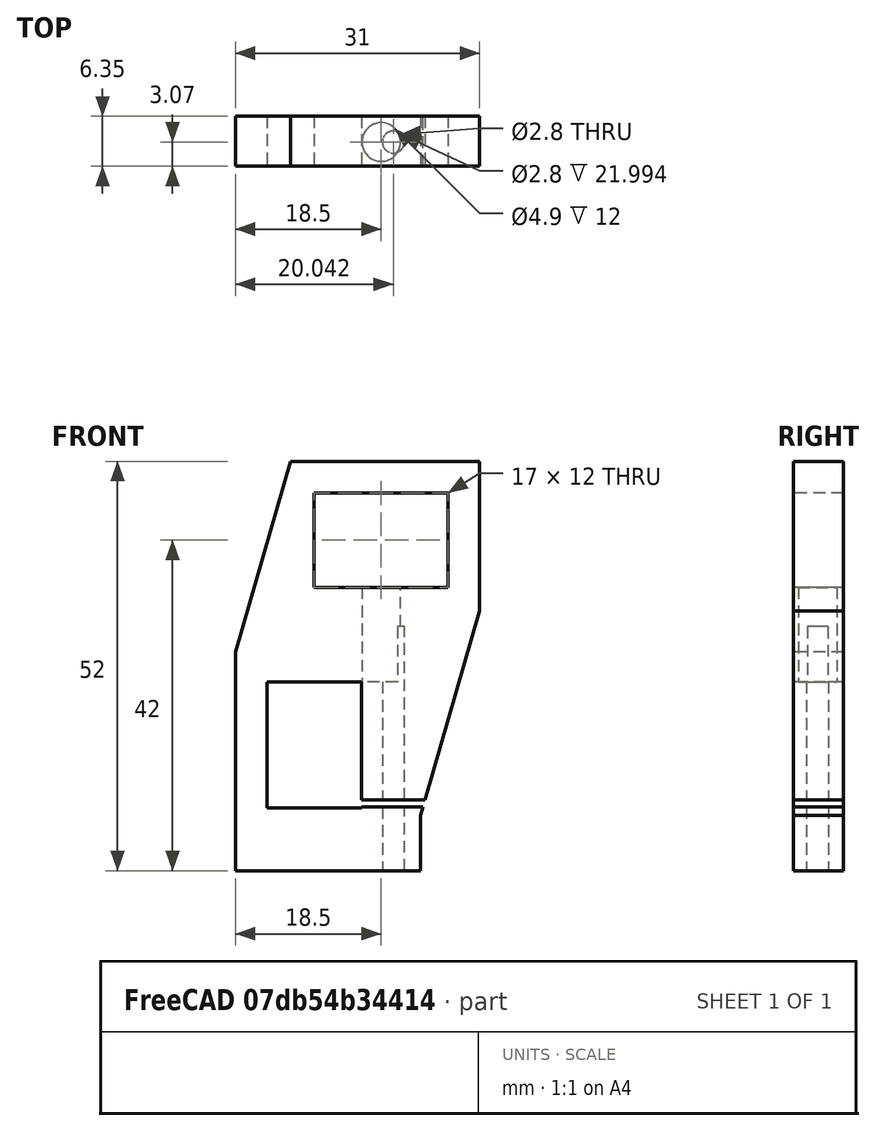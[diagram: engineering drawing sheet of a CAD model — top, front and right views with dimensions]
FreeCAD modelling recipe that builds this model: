
FCSTD DOCUMENT  (FreeCAD 0.19R)
Label: Tensioner_rail_clamp
License: All rights reserved
LicenseURL: http://en.wikipedia.org/wiki/All_rights_reserved
objects: Sketcher::SketchObject×4, PartDesign::Pocket×3, PartDesign::Pad×1, PartDesign::Body×1, Mesh::Feature×1
note: 13 computed .brp shape members not serialized (recipe doc carries the construction recipe); baked Part::Feature solids carry a one-line shape summary decoded from their .brp

FEATURE [Sketcher::SketchObject] Sketch
  FullyConstrained = false
  MapMode = 5
  Placement = pos=(0,0,0) rot=(1,0,0;1.5708rad)
  Support = -> [XZ_Plane]
  sketch-geometry (21):
    g0: LineSegment StartX=-8.5 StartY=6 StartZ=0 EndX=8.5 EndY=6 EndZ=0
    g1: LineSegment StartX=8.5 StartY=6 StartZ=0 EndX=8.5 EndY=-6 EndZ=0
    g2: LineSegment StartX=8.5 StartY=-6 StartZ=0 EndX=-8.5 EndY=-6 EndZ=0
    g3: LineSegment StartX=-8.5 StartY=-6 StartZ=0 EndX=-8.5 EndY=6 EndZ=0
    g4: LineSegment StartX=-11.5092 StartY=10 StartZ=0 EndX=12.5 EndY=10 EndZ=0
    g5: LineSegment StartX=12.5 StartY=10 StartZ=0 EndX=12.5 EndY=-9 EndZ=0
    g6: LineSegment StartX=5 StartY=-42 StartZ=0 EndX=-18.5 EndY=-42 EndZ=0
    g7: LineSegment StartX=-18.5 StartY=-42 StartZ=0 EndX=-18.5 EndY=-14.2346 EndZ=0
    g8: LineSegment StartX=-14.5 StartY=-18 StartZ=0 EndX=-2.5 EndY=-18 EndZ=0
    g9: LineSegment StartX=-2.5 StartY=-18 StartZ=0 EndX=-2.5 EndY=-34 EndZ=0
    g10: LineSegment StartX=-2.5 StartY=-34 StartZ=0 EndX=-14.5 EndY=-34 EndZ=0
    g11: LineSegment StartX=-14.5 StartY=-34 StartZ=0 EndX=-14.5 EndY=-18 EndZ=0
    g12: LineSegment StartX=-8.5 StartY=-12.9672 StartZ=0 EndX=-8.5 EndY=-37.1721 EndZ=0
    g13: LineSegment StartX=-22 StartY=-34 StartZ=0 EndX=5 EndY=-34 EndZ=0
    g14: LineSegment StartX=5 StartY=-34 StartZ=0 EndX=5 EndY=-46.7 EndZ=0
    g15: LineSegment StartX=5 StartY=-46.7 StartZ=0 EndX=-22 EndY=-46.7 EndZ=0
    g16: LineSegment StartX=-22 StartY=-46.7 StartZ=0 EndX=-22 EndY=-34 EndZ=0
    g17: LineSegment StartX=-8.5 StartY=-41.244 StartZ=0 EndX=-8.5 EndY=-73.7754 EndZ=0
    g18: LineSegment StartX=-18.5 StartY=-14.2346 StartZ=0 EndX=-11.5092 EndY=10 EndZ=0
    g19: LineSegment StartX=5 StartY=-42 StartZ=0 EndX=5 EndY=-35 EndZ=0
    g20: LineSegment StartX=5 StartY=-35 StartZ=0 EndX=12.5 EndY=-9 EndZ=0
  constraints (57):
    c: Coincident(g1,g2)
    c: Coincident(g2,g3)
    c: Coincident(g3,g0)
    c: Horizontal(g2)
    c: Vertical(g1)
    c: Distance(g0) = 17
    c: Coincident(g0,g1)
    c: Symmetric(g0,g2,g-1)
    c: Symmetric(g1,g0,g-1)
    c: Distance(g1) = 12
    c: Horizontal(g4)
    c: Coincident(g4,g5)
    c: Vertical(g5)
    c: Horizontal(g6)
    c: Coincident(g6,g7)
    c: Vertical(g7)
    c: Coincident(g8,g9)
    c: Coincident(g9,g10)
    c: Coincident(g10,g11)
    c: Coincident(g11,g8)
    c: Horizontal(g8)
    c: Horizontal(g10)
    c: Vertical(g9)
    c: Vertical(g11)
    c: Distance(g9) = 16
    c: Distance(g8) = 12
    c: Symmetric(g10,g9,g12)
    c: Coincident(g13,g14)
    c: Coincident(g14,g15)
    c: Coincident(g15,g16)
    c: Coincident(g16,g13)
    c: Horizontal(g13)
    c: Horizontal(g15)
    c: Vertical(g14)
    c: Vertical(g16)
    c: Symmetric(g13,g13,g17)
    c: Distance(g13) = 27
    c: Distance(g14) = 12.7
    c: DistanceX(g-1,g13) = 5
    c: PointOnObject(g12,g17)
    c: Distance(g10,g7) = 4
    c: Distance(g0,g4) = 4
    c: Distance(g9,g6) = 8
    c: Coincident(g7,g18)
    c: Coincident(g18,g4)
    c: Distance(g4,g1) = 4
    c: Coincident(g6,g19)
    c: Vertical(g19)
    c: Coincident(g19,g20)
    c: Coincident(g20,g5)
    c: Parallel(g20,g18)
    c: DistanceY(g8,g0) = 24
    c: Distance(g0,g18) = 4
    c: PointOnObject(g9,g13)
    c: DistanceX(g6) = 5
    c: DistanceY(g5) = -9
    c: DistanceY(g19) = -35
FEATURE [PartDesign::Pad] Pad
  Direction = (1,1,1)
  Length = 6.35
  Length2 = 100
  Placement = pos=(0,0,0) rot=(1,0,0;1.5708rad)
  Profile = -> Sketch
  Type = 0
FEATURE [Sketcher::SketchObject] Sketch001
  FullyConstrained = false
  MapMode = 5
  Placement = pos=(0,-6.35,4.2e-15) rot=(1,0,0;1.5708rad)
  Support = -> [Pad]
  sketch-geometry (4):
    g0: LineSegment StartX=-2.64152 StartY=-32.9944 StartZ=0 EndX=6.5725 EndY=-32.9944 EndZ=0
    g1: LineSegment StartX=6.5725 StartY=-32.9944 StartZ=0 EndX=6.5725 EndY=-33.8968 EndZ=0
    g2: LineSegment StartX=6.5725 StartY=-33.8968 StartZ=0 EndX=-2.64152 EndY=-33.8968 EndZ=0
    g3: LineSegment StartX=-2.64152 StartY=-33.8968 StartZ=0 EndX=-2.64152 EndY=-32.9944 EndZ=0
  constraints (8):
    c: Coincident(g0,g1)
    c: Coincident(g1,g2)
    c: Coincident(g2,g3)
    c: Coincident(g3,g0)
    c: Horizontal(g0)
    c: Horizontal(g2)
    c: Vertical(g1)
    c: Vertical(g3)
FEATURE [PartDesign::Pocket] Pocket
  BaseFeature = -> Pad
  Length = 5
  Length2 = 100
  Placement = pos=(0,0,0) rot=(1,0,0;1.5708rad)
  Profile = -> Sketch001
  Type = 1
FEATURE [Sketcher::SketchObject] Sketch002
  FullyConstrained = false
  MapMode = 5
  Placement = pos=(0,-4.66e-14,-42) rot=(1,0,0;3.14159rad)
  Support = -> [Pocket]
  sketch-geometry (1):
    g0: Circle CenterX=1.54184 CenterY=3.28 CenterZ=0 NormalX=0 NormalY=0 NormalZ=1 AngleXU=0 Radius=1.4
  constraints (2):
    c: DistanceY(g0) = 3.28
    c: Diameter(g0) = 2.8
FEATURE [PartDesign::Pocket] Pocket001
  BaseFeature = -> Pocket
  Length = 31
  Length2 = 100
  Placement = pos=(0,0,0) rot=(1,0,0;1.5708rad)
  Profile = -> Sketch002
  Type = 0
FEATURE [Sketcher::SketchObject] Sketch003
  FullyConstrained = true
  MapMode = 5
  Placement = pos=(0,-2.8e-14,-18) rot=(1,0,0;3.14159rad)
  Support = -> [Pocket001]
  sketch-geometry (1):
    g0: Circle CenterX=0 CenterY=3.28 CenterZ=0 NormalX=0 NormalY=0 NormalZ=1 AngleXU=0 Radius=2.45
  constraints (3):
    c: Diameter(g0) = 4.9
    c: PointOnObject(g0,g-2)
    c: DistanceY(g0) = 3.28
FEATURE [PartDesign::Pocket] Pocket002
  BaseFeature = -> Pocket001
  Length = 21
  Length2 = 100
  Placement = pos=(0,0,0) rot=(1,0,0;1.5708rad)
  Profile = -> Sketch003
  Type = 0
FEATURE [PartDesign::Body] Body
  Group = -> [Sketch,Pad,Sketch001,Pocket,Sketch002,Pocket001,Sketch003,Pocket002]
  Origin = -> Origin
  Tip = -> Pocket002
FEATURE [Mesh::Feature] Mesh  label="Pocket002 (Meshed)"
